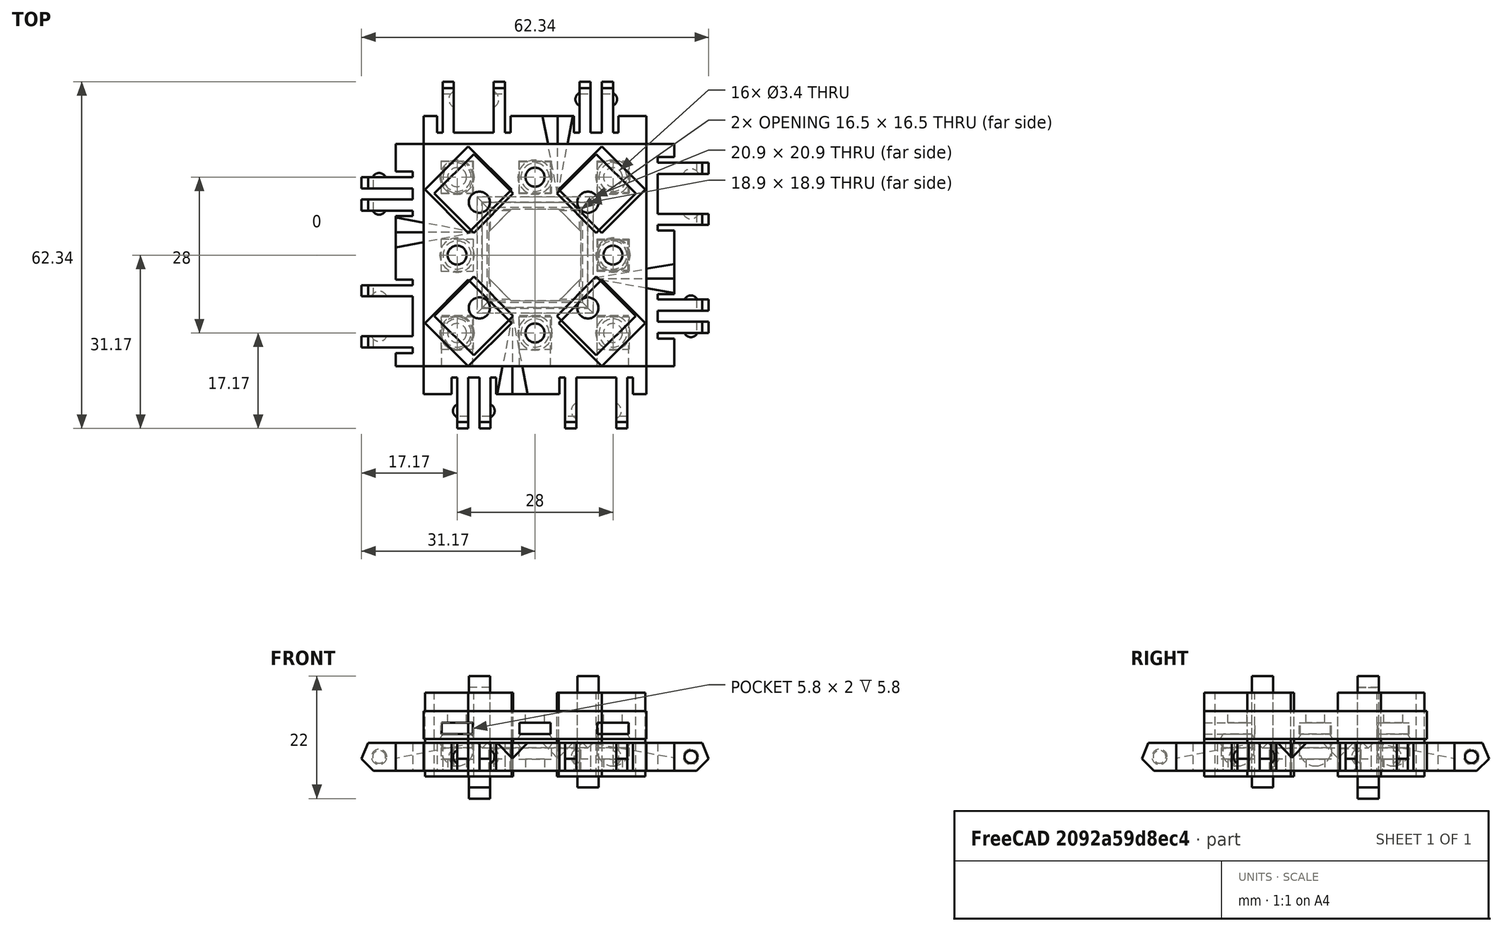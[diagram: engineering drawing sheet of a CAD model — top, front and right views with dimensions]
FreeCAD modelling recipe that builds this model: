
FCSTD DOCUMENT  (FreeCAD 0.17R13522 (Git))
Label: Robot Plates 0.2
License: All rights reserved
LicenseURL: http://en.wikipedia.org/wiki/All_rights_reserved
objects: Part::Box×147, Part::Sphere×51, Part::MultiFuse×48, Part::Cut×47, Part::Cylinder×24, Part::Chamfer×12, Part::Fuse×2, App::DocumentObjectGroup×1
note: 331 computed .brp shape members not serialized (recipe doc carries the construction recipe); baked Part::Feature solids carry a one-line shape summary decoded from their .brp

FEATURE [Part::Box] Box  label="Cube"
  AttacherType = Attacher::AttachEngine3D
  Height = 5
  Length = 40
  Placement = pos=(0,0,-2) rot=(0,0,1;0rad)
  Width = 40
FEATURE [Part::Sphere] Sphere003  label="Mag Hole 3"
  Angle1 = -90
  Angle2 = 90
  Angle3 = 360
  AttacherType = Attacher::AttachEngine3D
  Placement = pos=(6,34,1.7) rot=(0,0,1;0rad)
  Radius = 2.85
FEATURE [Part::Sphere] Sphere005  label="Mag Hole 2"
  Angle1 = -90
  Angle2 = 90
  Angle3 = 360
  AttacherType = Attacher::AttachEngine3D
  Placement = pos=(34,20,1.7) rot=(0,0,1;0rad)
  Radius = 2.85
FEATURE [Part::Sphere] Sphere  label="Mag Hole"
  Angle1 = -90
  Angle2 = 90
  Angle3 = 360
  AttacherType = Attacher::AttachEngine3D
  Placement = pos=(6,6,1.7) rot=(0,0,1;0rad)
  Radius = 2.85
FEATURE [Part::MultiFuse] Fusion004
  Shapes = -> [Sphere,Sphere005,Sphere003]
FEATURE [Part::Cut] Cut003
  Base = -> Box
  Tool = -> Fusion004
FEATURE [Part::Box] Box001  label="Cube001"
  AttacherType = Attacher::AttachEngine3D
  Height = 7
  Length = 5
  Width = 40
FEATURE [Part::Box] Box002  label="Cube002"
  AttacherType = Attacher::AttachEngine3D
  Height = 7
  Length = 10
  Placement = pos=(-10,6,0) rot=(0,0,1;0rad)
  Width = 2
FEATURE [Part::Box] Box003  label="Cube003"
  AttacherType = Attacher::AttachEngine3D
  Height = 7
  Length = 10
  Placement = pos=(-10,10,0) rot=(0,0,1;0rad)
  Width = 2
FEATURE [Part::Box] Box004  label="Cube004"
  AttacherType = Attacher::AttachEngine3D
  Height = 7
  Length = 10
  Placement = pos=(-10,25.4,0) rot=(0,0,1;0rad)
  Width = 2
FEATURE [Part::Box] Box005  label="Cube005"
  AttacherType = Attacher::AttachEngine3D
  Height = 7
  Length = 10
  Placement = pos=(-10,34.6,0) rot=(0,0,1;0rad)
  Width = 2
FEATURE [Part::Sphere] Sphere008
  Angle1 = -90
  Angle2 = 90
  Angle3 = 360
  AttacherType = Attacher::AttachEngine3D
  Placement = pos=(-3,6.5,2.5) rot=(0,0,1;0rad)
  Radius = 1.25
FEATURE [Part::Box] Box006  label="Cube006"
  AttacherType = Attacher::AttachEngine3D
  Height = 10
  Length = 13
  Placement = pos=(-10.19,0,-1.19) rot=(0,-1,0;0.785398rad)
  Width = 40
FEATURE [Part::Sphere] Sphere009
  Angle1 = -90
  Angle2 = 90
  Angle3 = 360
  AttacherType = Attacher::AttachEngine3D
  Placement = pos=(-3,11.5,2.5) rot=(0,0,1;0rad)
  Radius = 1.25
FEATURE [Part::Sphere] Sphere010
  Angle1 = -90
  Angle2 = 90
  Angle3 = 360
  AttacherType = Attacher::AttachEngine3D
  Placement = pos=(-3,28,2.5) rot=(0,0,1;0rad)
  Radius = 1.5
FEATURE [Part::Sphere] Sphere011
  Angle1 = -90
  Angle2 = 90
  Angle3 = 360
  AttacherType = Attacher::AttachEngine3D
  Placement = pos=(-3,34,2.5) rot=(0,0,1;0rad)
  Radius = 1.5
FEATURE [Part::MultiFuse] Fusion
  Shapes = -> [Box001,Box002,Box003,Box004,Box005]
FEATURE [Part::Cut] Cut
  Base = -> Fusion
  Tool = -> Box006
FEATURE [Part::MultiFuse] Fusion001
  Shapes = -> [Sphere008,Sphere009,Cut]
FEATURE [Part::MultiFuse] Fusion002
  Shapes = -> [Sphere011,Sphere010]
FEATURE [Part::Cut] Cut001
  Base = -> Fusion001
  Tool = -> Fusion002
FEATURE [Part::Chamfer] Chamfer001
  Base = -> Cut001
  Edges = 4 edges r=4: [Edge31,Edge37,Edge43,Edge46]
FEATURE [Part::Box] Box007  label="Cube007"
  AttacherType = Attacher::AttachEngine3D
  Height = 7
  Length = 4
  Placement = pos=(-1,5,0) rot=(0,0,1;0rad)
  Width = 1
FEATURE [Part::Box] Box008  label="Cube008"
  AttacherType = Attacher::AttachEngine3D
  Height = 7
  Length = 4
  Placement = pos=(-1,8,0) rot=(0,0,1;0rad)
  Width = 2
FEATURE [Part::Box] Box009  label="Cube009"
  AttacherType = Attacher::AttachEngine3D
  Height = 7
  Length = 4
  Placement = pos=(-1,12,0) rot=(0,0,1;0rad)
  Width = 1
FEATURE [Part::Box] Box010  label="Cube010"
  AttacherType = Attacher::AttachEngine3D
  Height = 7
  Length = 4
  Placement = pos=(-1,24.4,0) rot=(0,0,1;0rad)
  Width = 1
FEATURE [Part::Box] Box011  label="Cube011"
  AttacherType = Attacher::AttachEngine3D
  Height = 7
  Length = 4
  Placement = pos=(-1,36.6,0) rot=(0,0,1;0rad)
  Width = 1
FEATURE [Part::Box] Box012  label="Cube012"
  AttacherType = Attacher::AttachEngine3D
  Height = 7
  Length = 4
  Placement = pos=(-1,27.4,0) rot=(0,0,1;0rad)
  Width = 7.2
FEATURE [Part::MultiFuse] Fusion003
  Shapes = -> [Box012,Box009,Box011,Box008,Box010,Box007]
FEATURE [Part::Cut] Cut002
  Base = -> Chamfer001
  Placement = pos=(-5,40,3) rot=(1,0,0;3.14159rad)
  Tool = -> Fusion003
FEATURE [Part::Box] Box013  label="Cube013"
  AttacherType = Attacher::AttachEngine3D
  Height = 10
  Length = 12
  Placement = pos=(-11,-2,-12) rot=(0,0,1;0rad)
  Width = 44
FEATURE [Part::Cut] Cut004
  Base = -> Cut002
  Tool = -> Box013
FEATURE [Part::Box] Box014  label="Cube014"
  AttacherType = Attacher::AttachEngine3D
  Height = 7
  Length = 10
  Placement = pos=(-10,34.6,0) rot=(0,0,1;0rad)
  Width = 2
FEATURE [Part::Box] Box015  label="Cube015"
  AttacherType = Attacher::AttachEngine3D
  Height = 7
  Length = 5
  Width = 40
FEATURE [Part::Box] Box016  label="Cube016"
  AttacherType = Attacher::AttachEngine3D
  Height = 7
  Length = 10
  Placement = pos=(-10,25.4,0) rot=(0,0,1;0rad)
  Width = 2
FEATURE [Part::Box] Box017  label="Cube017"
  AttacherType = Attacher::AttachEngine3D
  Height = 7
  Length = 10
  Placement = pos=(-10,10,0) rot=(0,0,1;0rad)
  Width = 2
FEATURE [Part::Box] Box018  label="Cube018"
  AttacherType = Attacher::AttachEngine3D
  Height = 7
  Length = 10
  Placement = pos=(-10,6,0) rot=(0,0,1;0rad)
  Width = 2
FEATURE [Part::Sphere] Sphere012
  Angle1 = -90
  Angle2 = 90
  Angle3 = 360
  AttacherType = Attacher::AttachEngine3D
  Placement = pos=(-3,6.5,2.5) rot=(0,0,1;0rad)
  Radius = 1.25
FEATURE [Part::Box] Box019  label="Cube019"
  AttacherType = Attacher::AttachEngine3D
  Height = 10
  Length = 13
  Placement = pos=(-10.19,0,-1.19) rot=(0,-1,0;0.785398rad)
  Width = 40
FEATURE [Part::Sphere] Sphere013
  Angle1 = -90
  Angle2 = 90
  Angle3 = 360
  AttacherType = Attacher::AttachEngine3D
  Placement = pos=(-3,11.5,2.5) rot=(0,0,1;0rad)
  Radius = 1.25
FEATURE [Part::Sphere] Sphere014
  Angle1 = -90
  Angle2 = 90
  Angle3 = 360
  AttacherType = Attacher::AttachEngine3D
  Placement = pos=(-3,28,2.5) rot=(0,0,1;0rad)
  Radius = 1.5
FEATURE [Part::Sphere] Sphere015
  Angle1 = -90
  Angle2 = 90
  Angle3 = 360
  AttacherType = Attacher::AttachEngine3D
  Placement = pos=(-3,34,2.5) rot=(0,0,1;0rad)
  Radius = 1.5
FEATURE [Part::MultiFuse] Fusion005
  Shapes = -> [Box015,Box018,Box017,Box016,Box014]
FEATURE [Part::Cut] Cut005
  Base = -> Fusion005
  Tool = -> Box019
FEATURE [Part::MultiFuse] Fusion006
  Shapes = -> [Sphere012,Sphere013,Cut005]
FEATURE [Part::MultiFuse] Fusion007
  Shapes = -> [Sphere015,Sphere014]
FEATURE [Part::Cut] Cut006
  Base = -> Fusion006
  Tool = -> Fusion007
FEATURE [Part::Chamfer] Chamfer002
  Base = -> Cut006
  Edges = 4 edges r=4: [Edge31,Edge37,Edge43,Edge46]
FEATURE [Part::Box] Box020  label="Cube020"
  AttacherType = Attacher::AttachEngine3D
  Height = 7
  Length = 4
  Placement = pos=(-1,5,0) rot=(0,0,1;0rad)
  Width = 1
FEATURE [Part::Box] Box021  label="Cube021"
  AttacherType = Attacher::AttachEngine3D
  Height = 7
  Length = 4
  Placement = pos=(-1,8,0) rot=(0,0,1;0rad)
  Width = 2
FEATURE [Part::Box] Box022  label="Cube022"
  AttacherType = Attacher::AttachEngine3D
  Height = 7
  Length = 4
  Placement = pos=(-1,12,0) rot=(0,0,1;0rad)
  Width = 1
FEATURE [Part::Box] Box023  label="Cube023"
  AttacherType = Attacher::AttachEngine3D
  Height = 7
  Length = 4
  Placement = pos=(-1,24.4,0) rot=(0,0,1;0rad)
  Width = 1
FEATURE [Part::Box] Box024  label="Cube024"
  AttacherType = Attacher::AttachEngine3D
  Height = 7
  Length = 4
  Placement = pos=(-1,36.6,0) rot=(0,0,1;0rad)
  Width = 1
FEATURE [Part::Box] Box025  label="Cube025"
  AttacherType = Attacher::AttachEngine3D
  Height = 7
  Length = 4
  Placement = pos=(-1,27.4,0) rot=(0,0,1;0rad)
  Width = 7.2
FEATURE [Part::MultiFuse] Fusion008
  Shapes = -> [Box025,Box022,Box024,Box021,Box023,Box020]
FEATURE [Part::Cut] Cut007
  Base = -> Chamfer002
  Placement = pos=(-5,40,3) rot=(1,0,0;3.14159rad)
  Tool = -> Fusion008
FEATURE [Part::Box] Box026  label="Cube026"
  AttacherType = Attacher::AttachEngine3D
  Height = 10
  Length = 12
  Placement = pos=(-11,-2,-12) rot=(0,0,1;0rad)
  Width = 44
FEATURE [Part::Cut] Cut008
  Base = -> Cut007
  Placement = pos=(40,0,0) rot=(0,0,1;1.5708rad)
  Tool = -> Box026
FEATURE [Part::Box] Box027  label="Cube027"
  AttacherType = Attacher::AttachEngine3D
  Height = 7
  Length = 4
  Placement = pos=(-1,12,0) rot=(0,0,1;0rad)
  Width = 1
FEATURE [Part::Box] Box028  label="Cube028"
  AttacherType = Attacher::AttachEngine3D
  Height = 10
  Length = 13
  Placement = pos=(-10.19,0,-1.19) rot=(0,-1,0;0.785398rad)
  Width = 40
FEATURE [Part::Box] Box029  label="Cube029"
  AttacherType = Attacher::AttachEngine3D
  Height = 7
  Length = 4
  Placement = pos=(-1,27.4,0) rot=(0,0,1;0rad)
  Width = 7.2
FEATURE [Part::Box] Box030  label="Cube030"
  AttacherType = Attacher::AttachEngine3D
  Height = 7
  Length = 4
  Placement = pos=(-1,5,0) rot=(0,0,1;0rad)
  Width = 1
FEATURE [Part::Box] Box031  label="Cube031"
  AttacherType = Attacher::AttachEngine3D
  Height = 7
  Length = 10
  Placement = pos=(-10,6,0) rot=(0,0,1;0rad)
  Width = 2
FEATURE [Part::Box] Box032  label="Cube032"
  AttacherType = Attacher::AttachEngine3D
  Height = 10
  Length = 12
  Placement = pos=(-11,-2,-12) rot=(0,0,1;0rad)
  Width = 44
FEATURE [Part::Sphere] Sphere016
  Angle1 = -90
  Angle2 = 90
  Angle3 = 360
  AttacherType = Attacher::AttachEngine3D
  Placement = pos=(-3,6.5,2.5) rot=(0,0,1;0rad)
  Radius = 1.25
FEATURE [Part::Box] Box033  label="Cube033"
  AttacherType = Attacher::AttachEngine3D
  Height = 7
  Length = 10
  Placement = pos=(-10,25.4,0) rot=(0,0,1;0rad)
  Width = 2
FEATURE [Part::Box] Box034  label="Cube034"
  AttacherType = Attacher::AttachEngine3D
  Height = 7
  Length = 10
  Placement = pos=(-10,10,0) rot=(0,0,1;0rad)
  Width = 2
FEATURE [Part::Sphere] Sphere017
  Angle1 = -90
  Angle2 = 90
  Angle3 = 360
  AttacherType = Attacher::AttachEngine3D
  Placement = pos=(-3,28,2.5) rot=(0,0,1;0rad)
  Radius = 1.5
FEATURE [Part::Sphere] Sphere018
  Angle1 = -90
  Angle2 = 90
  Angle3 = 360
  AttacherType = Attacher::AttachEngine3D
  Placement = pos=(-3,11.5,2.5) rot=(0,0,1;0rad)
  Radius = 1.25
FEATURE [Part::Box] Box035  label="Cube035"
  AttacherType = Attacher::AttachEngine3D
  Height = 7
  Length = 4
  Placement = pos=(-1,36.6,0) rot=(0,0,1;0rad)
  Width = 1
FEATURE [Part::Sphere] Sphere019
  Angle1 = -90
  Angle2 = 90
  Angle3 = 360
  AttacherType = Attacher::AttachEngine3D
  Placement = pos=(-3,34,2.5) rot=(0,0,1;0rad)
  Radius = 1.5
FEATURE [Part::MultiFuse] Fusion011
  Shapes = -> [Sphere019,Sphere017]
FEATURE [Part::Box] Box036  label="Cube036"
  AttacherType = Attacher::AttachEngine3D
  Height = 7
  Length = 4
  Placement = pos=(-1,8,0) rot=(0,0,1;0rad)
  Width = 2
FEATURE [Part::Box] Box037  label="Cube037"
  AttacherType = Attacher::AttachEngine3D
  Height = 7
  Length = 10
  Placement = pos=(-10,34.6,0) rot=(0,0,1;0rad)
  Width = 2
FEATURE [Part::Box] Box038  label="Cube038"
  AttacherType = Attacher::AttachEngine3D
  Height = 7
  Length = 4
  Placement = pos=(-1,24.4,0) rot=(0,0,1;0rad)
  Width = 1
FEATURE [Part::MultiFuse] Fusion009
  Shapes = -> [Box029,Box027,Box035,Box036,Box038,Box030]
FEATURE [Part::Box] Box039  label="Cube039"
  AttacherType = Attacher::AttachEngine3D
  Height = 7
  Length = 5
  Width = 40
FEATURE [Part::MultiFuse] Fusion012
  Shapes = -> [Box039,Box031,Box034,Box033,Box037]
FEATURE [Part::Cut] Cut011
  Base = -> Fusion012
  Tool = -> Box028
FEATURE [Part::MultiFuse] Fusion010
  Shapes = -> [Sphere016,Sphere018,Cut011]
FEATURE [Part::Cut] Cut012
  Base = -> Fusion010
  Tool = -> Fusion011
FEATURE [Part::Chamfer] Chamfer003
  Base = -> Cut012
  Edges = 4 edges r=4: [Edge31,Edge37,Edge43,Edge46]
FEATURE [Part::Cut] Cut010
  Base = -> Chamfer003
  Placement = pos=(-5,40,3) rot=(1,0,0;3.14159rad)
  Tool = -> Fusion009
FEATURE [Part::Cut] Cut009
  Base = -> Cut010
  Placement = pos=(40,40,0) rot=(0,0,1;3.14159rad)
  Tool = -> Box032
FEATURE [Part::Sphere] Sphere020
  Angle1 = -90
  Angle2 = 90
  Angle3 = 360
  AttacherType = Attacher::AttachEngine3D
  Placement = pos=(-3,11.5,2.5) rot=(0,0,1;0rad)
  Radius = 1.25
FEATURE [Part::Box] Box040  label="Cube040"
  AttacherType = Attacher::AttachEngine3D
  Height = 7
  Length = 10
  Placement = pos=(-10,6,0) rot=(0,0,1;0rad)
  Width = 2
FEATURE [Part::Box] Box041  label="Cube041"
  AttacherType = Attacher::AttachEngine3D
  Height = 7
  Length = 4
  Placement = pos=(-1,8,0) rot=(0,0,1;0rad)
  Width = 2
FEATURE [Part::Box] Box042  label="Cube042"
  AttacherType = Attacher::AttachEngine3D
  Height = 7
  Length = 10
  Placement = pos=(-10,10,0) rot=(0,0,1;0rad)
  Width = 2
FEATURE [Part::Box] Box043  label="Cube043"
  AttacherType = Attacher::AttachEngine3D
  Height = 10
  Length = 12
  Placement = pos=(-11,-2,-12) rot=(0,0,1;0rad)
  Width = 44
FEATURE [Part::Box] Box044  label="Cube044"
  AttacherType = Attacher::AttachEngine3D
  Height = 7
  Length = 4
  Placement = pos=(-1,5,0) rot=(0,0,1;0rad)
  Width = 1
FEATURE [Part::Sphere] Sphere021
  Angle1 = -90
  Angle2 = 90
  Angle3 = 360
  AttacherType = Attacher::AttachEngine3D
  Placement = pos=(-3,28,2.5) rot=(0,0,1;0rad)
  Radius = 1.5
FEATURE [Part::Sphere] Sphere022
  Angle1 = -90
  Angle2 = 90
  Angle3 = 360
  AttacherType = Attacher::AttachEngine3D
  Placement = pos=(-3,6.5,2.5) rot=(0,0,1;0rad)
  Radius = 1.25
FEATURE [Part::Sphere] Sphere023
  Angle1 = -90
  Angle2 = 90
  Angle3 = 360
  AttacherType = Attacher::AttachEngine3D
  Placement = pos=(-3,34,2.5) rot=(0,0,1;0rad)
  Radius = 1.5
FEATURE [Part::Box] Box045  label="Cube045"
  AttacherType = Attacher::AttachEngine3D
  Height = 7
  Length = 4
  Placement = pos=(-1,12,0) rot=(0,0,1;0rad)
  Width = 1
FEATURE [Part::Box] Box046  label="Cube046"
  AttacherType = Attacher::AttachEngine3D
  Height = 7
  Length = 5
  Width = 40
FEATURE [Part::Box] Box047  label="Cube047"
  AttacherType = Attacher::AttachEngine3D
  Height = 7
  Length = 4
  Placement = pos=(-1,36.6,0) rot=(0,0,1;0rad)
  Width = 1
FEATURE [Part::Box] Box048  label="Cube048"
  AttacherType = Attacher::AttachEngine3D
  Height = 7
  Length = 4
  Placement = pos=(-1,24.4,0) rot=(0,0,1;0rad)
  Width = 1
FEATURE [Part::Box] Box049  label="Cube049"
  AttacherType = Attacher::AttachEngine3D
  Height = 7
  Length = 10
  Placement = pos=(-10,25.4,0) rot=(0,0,1;0rad)
  Width = 2
FEATURE [Part::Box] Box050  label="Cube050"
  AttacherType = Attacher::AttachEngine3D
  Height = 10
  Length = 13
  Placement = pos=(-10.19,0,-1.19) rot=(0,-1,0;0.785398rad)
  Width = 40
FEATURE [Part::Box] Box051  label="Cube051"
  AttacherType = Attacher::AttachEngine3D
  Height = 7
  Length = 10
  Placement = pos=(-10,34.6,0) rot=(0,0,1;0rad)
  Width = 2
FEATURE [Part::MultiFuse] Fusion015
  Shapes = -> [Box046,Box040,Box042,Box049,Box051]
FEATURE [Part::Cut] Cut013
  Base = -> Fusion015
  Tool = -> Box050
FEATURE [Part::MultiFuse] Fusion013
  Shapes = -> [Sphere022,Sphere020,Cut013]
FEATURE [Part::MultiFuse] Fusion016
  Shapes = -> [Sphere023,Sphere021]
FEATURE [Part::Cut] Cut014
  Base = -> Fusion013
  Tool = -> Fusion016
FEATURE [Part::Chamfer] Chamfer004
  Base = -> Cut014
  Edges = 4 edges r=4: [Edge31,Edge37,Edge43,Edge46]
FEATURE [Part::Box] Box052  label="Cube052"
  AttacherType = Attacher::AttachEngine3D
  Height = 7
  Length = 4
  Placement = pos=(-1,27.4,0) rot=(0,0,1;0rad)
  Width = 7.2
FEATURE [Part::MultiFuse] Fusion014
  Shapes = -> [Box052,Box045,Box047,Box041,Box048,Box044]
FEATURE [Part::Cut] Cut016
  Base = -> Chamfer004
  Placement = pos=(-5,40,3) rot=(1,0,0;3.14159rad)
  Tool = -> Fusion014
FEATURE [Part::Cut] Cut015
  Base = -> Cut016
  Placement = pos=(0,40,0) rot=(0,0,-1;1.5708rad)
  Tool = -> Box043
FEATURE [Part::Box] Box054  label="Cube054"
  AttacherType = Attacher::AttachEngine3D
  Height = 15
  Length = 10
  Placement = pos=(9,2,-3) rot=(0,0,1;0.785398rad)
  Width = 10
FEATURE [Part::Box] Box055  label="Cube055"
  AttacherType = Attacher::AttachEngine3D
  Height = 15
  Length = 10
  Placement = pos=(31,24,-3) rot=(0,0,1;0.785398rad)
  Width = 10
FEATURE [Part::Box] Box056  label="Cube056"
  AttacherType = Attacher::AttachEngine3D
  Height = 15
  Length = 10
  Placement = pos=(31,2,-3) rot=(0,0,1;0.785398rad)
  Width = 10
FEATURE [Part::Box] Box057  label="Cube057"
  AttacherType = Attacher::AttachEngine3D
  Height = 15
  Length = 10
  Placement = pos=(9,24,-3) rot=(0,0,1;0.785398rad)
  Width = 10
FEATURE [Part::MultiFuse] Fusion017
  Shapes = -> [Box054,Box057,Box056,Box055]
FEATURE [Part::Box] Box058  label="Cube058"
  AttacherType = Attacher::AttachEngine3D
  Height = 5
  Length = 40
  Placement = pos=(0,0,3.7) rot=(0,0,1;0rad)
  Width = 40
FEATURE [Part::Box] Box059  label="Square Nut Hole 008"
  AttacherType = Attacher::AttachEngine3D
  Height = 2
  Length = 5.6
  Placement = pos=(17.2,31.2,4.6) rot=(0,0,1;0rad)
  Width = 5.6
FEATURE [Part::Box] Box060  label="Square Nut Hole 009"
  AttacherType = Attacher::AttachEngine3D
  Height = 2
  Length = 5.6
  Placement = pos=(17.2,-0.85,4.6) rot=(0,0,1;0rad)
  Width = 10
FEATURE [Part::Box] Box061  label="Square Nut Hole 010"
  AttacherType = Attacher::AttachEngine3D
  Height = 2
  Length = 5.6
  Placement = pos=(31.2,-0.85,4.6) rot=(0,0,1;0rad)
  Width = 10
FEATURE [Part::Box] Box062  label="Square Nut Hole 011"
  AttacherType = Attacher::AttachEngine3D
  Height = 2
  Length = 5.4
  Placement = pos=(31.3,17.3,4.6) rot=(0,0,1;0rad)
  Width = 5.4
FEATURE [Part::Box] Box063  label="Square Nut Hole 012"
  AttacherType = Attacher::AttachEngine3D
  Height = 2
  Length = 5.7
  Placement = pos=(3.15,31.15,4.6) rot=(0,0,1;0rad)
  Width = 5.7
FEATURE [Part::Box] Box064  label="Square Nut Hole 013"
  AttacherType = Attacher::AttachEngine3D
  Height = 2
  Length = 5.5
  Placement = pos=(31.25,31.25,4.6) rot=(0,0,1;0rad)
  Width = 5.5
FEATURE [Part::Box] Box065  label="Square Nut Hole 014"
  AttacherType = Attacher::AttachEngine3D
  Height = 2
  Length = 5.8
  Placement = pos=(3.1,17.1,4.6) rot=(0,0,1;0rad)
  Width = 5.8
FEATURE [Part::Box] Box066  label="Square Nut Hole 015"
  AttacherType = Attacher::AttachEngine3D
  Height = 2
  Length = 5.6
  Placement = pos=(3.2,-0.85,4.6) rot=(0,0,1;0rad)
  Width = 10
FEATURE [Part::Sphere] Sphere006  label="Nut Clearence1"
  Angle1 = -90
  Angle2 = 90
  Angle3 = 360
  AttacherType = Attacher::AttachEngine3D
  Placement = pos=(6,6,2.4) rot=(0,0,1;0rad)
  Radius = 3.35
FEATURE [Part::Sphere] Sphere024
  Angle1 = -90
  Angle2 = 90
  Angle3 = 360
  AttacherType = Attacher::AttachEngine3D
  Placement = pos=(6,34,2.4) rot=(0,0,1;0rad)
  Radius = 3.35
FEATURE [Part::Sphere] Sphere007
  Angle1 = -90
  Angle2 = 90
  Angle3 = 360
  AttacherType = Attacher::AttachEngine3D
  Placement = pos=(34,20,2.4) rot=(0,0,1;0rad)
  Radius = 3.35
FEATURE [Part::Sphere] Sphere001
  Angle1 = -90
  Angle2 = 90
  Angle3 = 360
  AttacherType = Attacher::AttachEngine3D
  Placement = pos=(34,6,2.4) rot=(0,0,1;0rad)
  Radius = 3.35
FEATURE [Part::Sphere] Sphere025
  Angle1 = -90
  Angle2 = 90
  Angle3 = 360
  AttacherType = Attacher::AttachEngine3D
  Placement = pos=(20,6,2.4) rot=(0,0,1;0rad)
  Radius = 3.35
FEATURE [Part::Sphere] Sphere026
  Angle1 = -90
  Angle2 = 90
  Angle3 = 360
  AttacherType = Attacher::AttachEngine3D
  Placement = pos=(20,34,2.4) rot=(0,0,1;0rad)
  Radius = 3.35
FEATURE [Part::Sphere] Sphere004
  Angle1 = -90
  Angle2 = 90
  Angle3 = 360
  AttacherType = Attacher::AttachEngine3D
  Placement = pos=(6,20,2.4) rot=(0,0,1;0rad)
  Radius = 3.35
FEATURE [Part::Sphere] Sphere002
  Angle1 = -90
  Angle2 = 90
  Angle3 = 360
  AttacherType = Attacher::AttachEngine3D
  Placement = pos=(34,34,2.4) rot=(0,0,1;0rad)
  Radius = 3.35
FEATURE [Part::Cylinder] Cylinder
  Angle = 360
  AttacherType = Attacher::AttachEngine3D
  Height = 10
  Placement = pos=(6,6,0) rot=(0,0,1;0rad)
  Radius = 1.7
FEATURE [Part::Cylinder] Cylinder002
  Angle = 360
  AttacherType = Attacher::AttachEngine3D
  Height = 10
  Placement = pos=(34,6,0) rot=(0,0,1;0rad)
  Radius = 1.7
FEATURE [Part::Cylinder] Cylinder001
  Angle = 360
  AttacherType = Attacher::AttachEngine3D
  Height = 10
  Placement = pos=(20,6,0) rot=(0,0,1;0rad)
  Radius = 1.7
FEATURE [Part::Cylinder] Cylinder003
  Angle = 360
  AttacherType = Attacher::AttachEngine3D
  Height = 10
  Placement = pos=(34,34,0) rot=(0,0,1;0rad)
  Radius = 1.7
FEATURE [Part::Cylinder] Cylinder004
  Angle = 360
  AttacherType = Attacher::AttachEngine3D
  Height = 10
  Placement = pos=(20,34,0) rot=(0,0,1;0rad)
  Radius = 1.7
FEATURE [Part::Cylinder] Cylinder005
  Angle = 360
  AttacherType = Attacher::AttachEngine3D
  Height = 10
  Placement = pos=(6,34,0) rot=(0,0,1;0rad)
  Radius = 1.7
FEATURE [Part::Cylinder] Cylinder006
  Angle = 360
  AttacherType = Attacher::AttachEngine3D
  Height = 10
  Placement = pos=(6,20,0) rot=(0,0,1;0rad)
  Radius = 1.7
FEATURE [Part::Cylinder] Cylinder007
  Angle = 360
  AttacherType = Attacher::AttachEngine3D
  Height = 10
  Placement = pos=(34,20,0) rot=(0,0,1;0rad)
  Radius = 1.7
FEATURE [Part::MultiFuse] Fusion018
  Shapes = -> [Cylinder,Cylinder004,Cylinder007,Cylinder005,Cylinder006,Cylinder001,Cylinder002,Cylinder003]
FEATURE [Part::MultiFuse] Fusion019
  Shapes = -> [Sphere007,Sphere024,Sphere006,Sphere025,Sphere001,Sphere026,Sphere004,Sphere002]
FEATURE [Part::MultiFuse] Fusion020
  Shapes = -> [Box061,Box065,Box062,Box063,Box064,Box066,Box059,Box060]
FEATURE [Part::Cut] Cut017
  Base = -> Box058
  Tool = -> Fusion020
FEATURE [Part::Cut] Cut019
  Base = -> Cut017
  Tool = -> Fusion019
FEATURE [Part::Cut] Cut018
  Base = -> Cut019
  Tool = -> Fusion018
FEATURE [Part::Cylinder] Cylinder008
  Angle = 360
  AttacherType = Attacher::AttachEngine3D
  Height = 20
  Placement = pos=(10,10.5,-5) rot=(0,0,1;0rad)
  Radius = 1.9
FEATURE [Part::Cylinder] Cylinder009
  Angle = 360
  AttacherType = Attacher::AttachEngine3D
  Height = 20
  Placement = pos=(29.5,10.5,-5) rot=(0,0,1;0rad)
  Radius = 1.9
FEATURE [Part::Cylinder] Cylinder010
  Angle = 360
  AttacherType = Attacher::AttachEngine3D
  Height = 20
  Placement = pos=(29.5,29.5,-5) rot=(0,0,1;0rad)
  Radius = 1.9
FEATURE [Part::Cylinder] Cylinder011
  Angle = 360
  AttacherType = Attacher::AttachEngine3D
  Height = 20
  Placement = pos=(10,29.5,-7) rot=(0,0,1;0rad)
  Radius = 1.9
FEATURE [Part::MultiFuse] Fusion021  label="M2 Screw holes"
  Shapes = -> [Cylinder008,Cylinder009,Cylinder011,Cylinder010]
FEATURE [Part::Box] Box067  label="Square Nut Hole 016"
  AttacherType = Attacher::AttachEngine3D
  Height = 2
  Length = 5.8
  Placement = pos=(31.1,17.1,4.6) rot=(0,0,1;0rad)
  Width = 5.8
FEATURE [Part::Box] Box068  label="Square Nut Hole 017"
  AttacherType = Attacher::AttachEngine3D
  Height = 2
  Length = 5.8
  Placement = pos=(17.1,3.1,4.6) rot=(0,0,1;0rad)
  Width = 5.8
FEATURE [Part::Box] Box069  label="Square Nut Hole 018"
  AttacherType = Attacher::AttachEngine3D
  Height = 2
  Length = 5.8
  Placement = pos=(31.1,3.1,4.6) rot=(0,0,1;0rad)
  Width = 5.8
FEATURE [Part::Box] Box070  label="Square Nut Hole 019"
  AttacherType = Attacher::AttachEngine3D
  Height = 2
  Length = 5.8
  Placement = pos=(3.1,3.1,4.6) rot=(0,0,1;0rad)
  Width = 5.8
FEATURE [Part::Box] Box071  label="Square Nut Hole 020"
  AttacherType = Attacher::AttachEngine3D
  Height = 2
  Length = 5.8
  Placement = pos=(3.1,31.1,4.6) rot=(0,0,1;0rad)
  Width = 5.8
FEATURE [Part::Box] Box072  label="Square Nut Hole 021"
  AttacherType = Attacher::AttachEngine3D
  Height = 2
  Length = 5.8
  Placement = pos=(17.1,31.1,4.6) rot=(0,0,1;0rad)
  Width = 5.8
FEATURE [Part::Box] Box073  label="Square Nut Hole 022"
  AttacherType = Attacher::AttachEngine3D
  Height = 2
  Length = 5.8
  Placement = pos=(31.1,31.1,4.6) rot=(0,0,1;0rad)
  Width = 5.8
FEATURE [Part::Box] Box074  label="Square Nut Hole 023"
  AttacherType = Attacher::AttachEngine3D
  Height = 2
  Length = 5.8
  Placement = pos=(3.1,17.1,4.6) rot=(0,0,1;0rad)
  Width = 5.8
FEATURE [Part::Cylinder] Cylinder012
  Angle = 360
  AttacherType = Attacher::AttachEngine3D
  Height = 10
  Placement = pos=(6,6,0) rot=(0,0,1;0rad)
  Radius = 1.7
FEATURE [Part::Cylinder] Cylinder013
  Angle = 360
  AttacherType = Attacher::AttachEngine3D
  Height = 10
  Placement = pos=(34,34,0) rot=(0,0,1;0rad)
  Radius = 1.7
FEATURE [Part::Cylinder] Cylinder014
  Angle = 360
  AttacherType = Attacher::AttachEngine3D
  Height = 10
  Placement = pos=(20,34,0) rot=(0,0,1;0rad)
  Radius = 1.7
FEATURE [Part::Cylinder] Cylinder015
  Angle = 360
  AttacherType = Attacher::AttachEngine3D
  Height = 10
  Placement = pos=(6,34,0) rot=(0,0,1;0rad)
  Radius = 1.7
FEATURE [Part::Cylinder] Cylinder016
  Angle = 360
  AttacherType = Attacher::AttachEngine3D
  Height = 10
  Placement = pos=(6,20,0) rot=(0,0,1;0rad)
  Radius = 1.7
FEATURE [Part::Cylinder] Cylinder017
  Angle = 360
  AttacherType = Attacher::AttachEngine3D
  Height = 10
  Placement = pos=(34,20,0) rot=(0,0,1;0rad)
  Radius = 1.7
FEATURE [Part::Cylinder] Cylinder018
  Angle = 360
  AttacherType = Attacher::AttachEngine3D
  Height = 10
  Placement = pos=(34,6,0) rot=(0,0,1;0rad)
  Radius = 1.7
FEATURE [Part::Cylinder] Cylinder019
  Angle = 360
  AttacherType = Attacher::AttachEngine3D
  Height = 10
  Placement = pos=(20,6,0) rot=(0,0,1;0rad)
  Radius = 1.7
FEATURE [Part::Box] Box075  label="Cube059"
  AttacherType = Attacher::AttachEngine3D
  Height = 5
  Length = 40
  Placement = pos=(0,0,-2) rot=(0,0,1;0rad)
  Width = 40
FEATURE [Part::Sphere] Sphere027
  Angle1 = -90
  Angle2 = 90
  Angle3 = 360
  AttacherType = Attacher::AttachEngine3D
  Placement = pos=(34,20,2.4) rot=(0,0,1;0rad)
  Radius = 3.35
FEATURE [Part::Sphere] Sphere028  label="Nut Clearence002"
  Angle1 = -90
  Angle2 = 90
  Angle3 = 360
  AttacherType = Attacher::AttachEngine3D
  Placement = pos=(6,6,2.4) rot=(0,0,1;0rad)
  Radius = 3.35
FEATURE [Part::Sphere] Sphere029
  Angle1 = -90
  Angle2 = 90
  Angle3 = 360
  AttacherType = Attacher::AttachEngine3D
  Placement = pos=(34,34,2.4) rot=(0,0,1;0rad)
  Radius = 3.35
FEATURE [Part::Sphere] Sphere030
  Angle1 = -90
  Angle2 = 90
  Angle3 = 360
  AttacherType = Attacher::AttachEngine3D
  Placement = pos=(34,6,2.4) rot=(0,0,1;0rad)
  Radius = 3.35
FEATURE [Part::Sphere] Sphere031
  Angle1 = -90
  Angle2 = 90
  Angle3 = 360
  AttacherType = Attacher::AttachEngine3D
  Placement = pos=(20,6,2.4) rot=(0,0,1;0rad)
  Radius = 3.35
FEATURE [Part::Sphere] Sphere032
  Angle1 = -90
  Angle2 = 90
  Angle3 = 360
  AttacherType = Attacher::AttachEngine3D
  Placement = pos=(6,34,2.4) rot=(0,0,1;0rad)
  Radius = 3.35
FEATURE [Part::Sphere] Sphere033
  Angle1 = -90
  Angle2 = 90
  Angle3 = 360
  AttacherType = Attacher::AttachEngine3D
  Placement = pos=(6,20,2.4) rot=(0,0,1;0rad)
  Radius = 3.35
FEATURE [Part::Sphere] Sphere034
  Angle1 = -90
  Angle2 = 90
  Angle3 = 360
  AttacherType = Attacher::AttachEngine3D
  Placement = pos=(20,34,2.4) rot=(0,0,1;0rad)
  Radius = 3.35
FEATURE [Part::Box] Box076  label="Cube060"
  AttacherType = Attacher::AttachEngine3D
  Height = 15
  Length = 16.5
  Placement = pos=(11.75,11.75,-3) rot=(0,0,1;0rad)
  Width = 16.5
FEATURE [Part::Box] Box077  label="Cube061"
  AttacherType = Attacher::AttachEngine3D
  Height = 15
  Length = 11
  Placement = pos=(8,24,-3) rot=(0,0,1;0.785398rad)
  Width = 11
FEATURE [Part::Box] Box078  label="Cube062"
  AttacherType = Attacher::AttachEngine3D
  Height = 15
  Length = 11
  Placement = pos=(8,0,-3) rot=(0,0,1;0.785398rad)
  Width = 11
FEATURE [Part::Box] Box079  label="Cube063"
  AttacherType = Attacher::AttachEngine3D
  Height = 15
  Length = 11
  Placement = pos=(32,0,-3) rot=(0,0,1;0.785398rad)
  Width = 11
FEATURE [Part::Box] Box080  label="Cube064"
  AttacherType = Attacher::AttachEngine3D
  Height = 15
  Length = 11
  Placement = pos=(32,24,-3) rot=(0,0,1;0.785398rad)
  Width = 11
FEATURE [Part::MultiFuse] Fusion022
  Shapes = -> [Box078,Box077,Box079,Box080]
FEATURE [Part::Cylinder] Cylinder020
  Angle = 360
  AttacherType = Attacher::AttachEngine3D
  Height = 20
  Placement = pos=(29.5,10.5,-5) rot=(0,0,1;0rad)
  Radius = 1.9
FEATURE [Part::Cylinder] Cylinder021
  Angle = 360
  AttacherType = Attacher::AttachEngine3D
  Height = 20
  Placement = pos=(10,29.5,-7) rot=(0,0,1;0rad)
  Radius = 1.9
FEATURE [Part::Cylinder] Cylinder022
  Angle = 360
  AttacherType = Attacher::AttachEngine3D
  Height = 20
  Placement = pos=(10,10.5,-5) rot=(0,0,1;0rad)
  Radius = 1.9
FEATURE [Part::Cylinder] Cylinder023
  Angle = 360
  AttacherType = Attacher::AttachEngine3D
  Height = 20
  Placement = pos=(29.5,29.5,-5) rot=(0,0,1;0rad)
  Radius = 1.9
FEATURE [Part::MultiFuse] Fusion023  label="M2 Screw holes001"
  Shapes = -> [Cylinder022,Cylinder020,Cylinder021,Cylinder023]
FEATURE [Part::MultiFuse] Fusion024  label="Square Nut Hole"
  Shapes = -> [Box067,Box073,Box071,Box069,Box068,Box070,Box072,Box074]
FEATURE [Part::MultiFuse] Fusion025  label="Square Nut Screw Holes"
  Shapes = -> [Cylinder012,Cylinder018,Cylinder016,Cylinder015,Cylinder014,Cylinder013,Cylinder017,Cylinder019]
FEATURE [Part::MultiFuse] Fusion026  label="Nut Chamfers"
  Shapes = -> [Sphere027,Sphere028,Sphere029,Sphere031,Sphere032,Sphere033,Sphere034,Sphere030]
FEATURE [App::DocumentObjectGroup] Group  label="Cubes"
  Group = -> [Fusion017,Fusion022]
FEATURE [Part::Box] Box082  label="Cube066"
  AttacherType = Attacher::AttachEngine3D
  Height = 10
  Length = 15
  Placement = pos=(30.8481,15.8,2.86019) rot=(0.974848,0.205904,-0.085288;0.803573rad)
  Width = 10
FEATURE [Part::Box] Box083  label="Cube067"
  AttacherType = Attacher::AttachEngine3D
  Height = 10
  Length = 21
  Placement = pos=(9.5,9.5,2.1) rot=(0,0,1;0rad)
  Width = 21
FEATURE [Part::Box] Box084  label="Cube068"
  AttacherType = Attacher::AttachEngine3D
  Height = 14
  Length = 17
  Placement = pos=(11.5,11.5,0) rot=(0,0,1;0rad)
  Width = 17
FEATURE [Part::Cut] Cut020
  Base = -> Box083
  Tool = -> Box084
FEATURE [Part::Chamfer] Chamfer007
  Base = -> Cut020
  Edges = 8 edges r=0.95: [Edge4,Edge5,Edge14,Edge16,Edge17,Edge18,Edge19,Edge20]
FEATURE [Part::Chamfer] Chamfer008
  Base = -> Box076
  Edges = 4 edges r=4: [Edge1,Edge3,Edge5,Edge7]
FEATURE [Part::Box] Box085  label="Cube069"
  AttacherType = Attacher::AttachEngine3D
  Height = 15
  Length = 16
  Placement = pos=(12,12,-13) rot=(0,0,1;0rad)
  Width = 16
FEATURE [Part::Box] Box086  label="Cube070"
  AttacherType = Attacher::AttachEngine3D
  Height = 10
  Length = 10
  Placement = pos=(17,32.0919,9.95) rot=(-0.225436,0.969773,-0.093378;0.807337rad)
  Width = 15
FEATURE [Part::Box] Box087  label="Cube071"
  AttacherType = Attacher::AttachEngine3D
  Height = 10
  Length = 10
  Placement = pos=(7.9081,17,9.95) rot=(-0.450607,0.280623,0.847469;1.65638rad)
  Width = 15
FEATURE [Part::Box] Box088  label="Cube072"
  AttacherType = Attacher::AttachEngine3D
  Height = 10
  Length = 10
  Placement = pos=(23,7.9081,9.95) rot=(-0.381178,-0.08861,0.920245;3.06822rad)
  Width = 15
FEATURE [Part::MultiFuse] Fusion027
  Shapes = -> [Box086,Box082,Box087,Box088]
FEATURE [Part::MultiFuse] Fusion028
  Shapes = -> [Cut015,Cut004,Cut008,Cut009]
FEATURE [Part::Box] Box089  label="Cube073"
  AttacherType = Attacher::AttachEngine3D
  Height = 10
  Length = 10
  Placement = pos=(17,32.0919,9.95) rot=(-0.225436,0.969773,-0.093378;0.807337rad)
  Width = 15
FEATURE [Part::Box] Box090  label="Cube074"
  AttacherType = Attacher::AttachEngine3D
  Height = 10
  Length = 15
  Placement = pos=(30.8481,15.8,2.86019) rot=(0.974848,0.205904,-0.085288;0.803573rad)
  Width = 10
FEATURE [Part::Box] Box091  label="Cube075"
  AttacherType = Attacher::AttachEngine3D
  Height = 10
  Length = 10
  Placement = pos=(7.9081,17,9.95) rot=(-0.450607,0.280623,0.847469;1.65638rad)
  Width = 15
FEATURE [Part::Box] Box092  label="Cube076"
  AttacherType = Attacher::AttachEngine3D
  Height = 10
  Length = 10
  Placement = pos=(23,7.9081,9.95) rot=(-0.381178,-0.08861,0.920245;3.06822rad)
  Width = 15
FEATURE [Part::Box] Box093  label="Cube077"
  AttacherType = Attacher::AttachEngine3D
  Height = 7
  Length = 5
  Width = 40
FEATURE [Part::Box] Box094  label="Cube078"
  AttacherType = Attacher::AttachEngine3D
  Height = 7
  Length = 10
  Placement = pos=(-10,6,0) rot=(0,0,1;0rad)
  Width = 2
FEATURE [Part::Box] Box095  label="Cube079"
  AttacherType = Attacher::AttachEngine3D
  Height = 7
  Length = 10
  Placement = pos=(-10,10,0) rot=(0,0,1;0rad)
  Width = 2
FEATURE [Part::Box] Box096  label="Cube080"
  AttacherType = Attacher::AttachEngine3D
  Height = 7
  Length = 10
  Placement = pos=(-10,25.4,0) rot=(0,0,1;0rad)
  Width = 2
FEATURE [Part::Box] Box097  label="Cube081"
  AttacherType = Attacher::AttachEngine3D
  Height = 7
  Length = 10
  Placement = pos=(-10,34.6,0) rot=(0,0,1;0rad)
  Width = 2
FEATURE [Part::Sphere] Sphere035
  Angle1 = -90
  Angle2 = 90
  Angle3 = 360
  AttacherType = Attacher::AttachEngine3D
  Placement = pos=(-3,6.5,2.5) rot=(0,0,1;0rad)
  Radius = 1.25
FEATURE [Part::Box] Box098  label="Cube082"
  AttacherType = Attacher::AttachEngine3D
  Height = 10
  Length = 13
  Placement = pos=(-10.19,0,-1.19) rot=(0,-1,0;0.785398rad)
  Width = 40
FEATURE [Part::Sphere] Sphere036
  Angle1 = -90
  Angle2 = 90
  Angle3 = 360
  AttacherType = Attacher::AttachEngine3D
  Placement = pos=(-3,11.5,2.5) rot=(0,0,1;0rad)
  Radius = 1.25
FEATURE [Part::Sphere] Sphere037
  Angle1 = -90
  Angle2 = 90
  Angle3 = 360
  AttacherType = Attacher::AttachEngine3D
  Placement = pos=(-3,28,2.5) rot=(0,0,1;0rad)
  Radius = 1.5
FEATURE [Part::Sphere] Sphere038
  Angle1 = -90
  Angle2 = 90
  Angle3 = 360
  AttacherType = Attacher::AttachEngine3D
  Placement = pos=(-3,34,2.5) rot=(0,0,1;0rad)
  Radius = 1.5
FEATURE [Part::MultiFuse] Fusion030
  Shapes = -> [Box093,Box094,Box095,Box096,Box097]
FEATURE [Part::Cut] Cut025
  Base = -> Fusion030
  Tool = -> Box098
FEATURE [Part::MultiFuse] Fusion031
  Shapes = -> [Sphere035,Sphere036,Cut025]
FEATURE [Part::MultiFuse] Fusion032
  Shapes = -> [Sphere038,Sphere037]
FEATURE [Part::Cut] Cut026
  Base = -> Fusion031
  Tool = -> Fusion032
FEATURE [Part::Chamfer] Chamfer009
  Base = -> Cut026
  Edges = 4 edges r=4: [Edge31,Edge37,Edge43,Edge46]
FEATURE [Part::Box] Box099  label="Cube083"
  AttacherType = Attacher::AttachEngine3D
  Height = 7
  Length = 4
  Placement = pos=(-1,5,0) rot=(0,0,1;0rad)
  Width = 1
FEATURE [Part::Box] Box100  label="Cube084"
  AttacherType = Attacher::AttachEngine3D
  Height = 7
  Length = 4
  Placement = pos=(-1,8,0) rot=(0,0,1;0rad)
  Width = 2
FEATURE [Part::Box] Box101  label="Cube085"
  AttacherType = Attacher::AttachEngine3D
  Height = 7
  Length = 4
  Placement = pos=(-1,12,0) rot=(0,0,1;0rad)
  Width = 1
FEATURE [Part::Box] Box102  label="Cube086"
  AttacherType = Attacher::AttachEngine3D
  Height = 7
  Length = 4
  Placement = pos=(-1,24.4,0) rot=(0,0,1;0rad)
  Width = 1
FEATURE [Part::Box] Box103  label="Cube087"
  AttacherType = Attacher::AttachEngine3D
  Height = 7
  Length = 4
  Placement = pos=(-1,36.6,0) rot=(0,0,1;0rad)
  Width = 1
FEATURE [Part::Box] Box104  label="Cube088"
  AttacherType = Attacher::AttachEngine3D
  Height = 7
  Length = 4
  Placement = pos=(-1,27.4,0) rot=(0,0,1;0rad)
  Width = 7.2
FEATURE [Part::MultiFuse] Fusion033
  Shapes = -> [Box104,Box101,Box103,Box100,Box102,Box099]
FEATURE [Part::Cut] Cut027
  Base = -> Chamfer009
  Placement = pos=(-5,40,3) rot=(1,0,0;3.14159rad)
  Tool = -> Fusion033
FEATURE [Part::Box] Box105  label="Cube089"
  AttacherType = Attacher::AttachEngine3D
  Height = 10
  Length = 12
  Placement = pos=(-11,-2,-12) rot=(0,0,1;0rad)
  Width = 44
FEATURE [Part::Cut] Cut028
  Base = -> Cut027
  Tool = -> Box105
FEATURE [Part::Box] Box106  label="Cube090"
  AttacherType = Attacher::AttachEngine3D
  Height = 7
  Length = 10
  Placement = pos=(-10,34.6,0) rot=(0,0,1;0rad)
  Width = 2
FEATURE [Part::Box] Box107  label="Cube091"
  AttacherType = Attacher::AttachEngine3D
  Height = 7
  Length = 5
  Width = 40
FEATURE [Part::Box] Box108  label="Cube092"
  AttacherType = Attacher::AttachEngine3D
  Height = 7
  Length = 10
  Placement = pos=(-10,25.4,0) rot=(0,0,1;0rad)
  Width = 2
FEATURE [Part::Box] Box109  label="Cube093"
  AttacherType = Attacher::AttachEngine3D
  Height = 7
  Length = 10
  Placement = pos=(-10,10,0) rot=(0,0,1;0rad)
  Width = 2
FEATURE [Part::Box] Box110  label="Cube094"
  AttacherType = Attacher::AttachEngine3D
  Height = 7
  Length = 10
  Placement = pos=(-10,6,0) rot=(0,0,1;0rad)
  Width = 2
FEATURE [Part::Sphere] Sphere039
  Angle1 = -90
  Angle2 = 90
  Angle3 = 360
  AttacherType = Attacher::AttachEngine3D
  Placement = pos=(-3,6.5,2.5) rot=(0,0,1;0rad)
  Radius = 1.25
FEATURE [Part::Box] Box111  label="Cube095"
  AttacherType = Attacher::AttachEngine3D
  Height = 10
  Length = 13
  Placement = pos=(-10.19,0,-1.19) rot=(0,-1,0;0.785398rad)
  Width = 40
FEATURE [Part::Sphere] Sphere040
  Angle1 = -90
  Angle2 = 90
  Angle3 = 360
  AttacherType = Attacher::AttachEngine3D
  Placement = pos=(-3,11.5,2.5) rot=(0,0,1;0rad)
  Radius = 1.25
FEATURE [Part::Sphere] Sphere041
  Angle1 = -90
  Angle2 = 90
  Angle3 = 360
  AttacherType = Attacher::AttachEngine3D
  Placement = pos=(-3,28,2.5) rot=(0,0,1;0rad)
  Radius = 1.5
FEATURE [Part::Sphere] Sphere042
  Angle1 = -90
  Angle2 = 90
  Angle3 = 360
  AttacherType = Attacher::AttachEngine3D
  Placement = pos=(-3,34,2.5) rot=(0,0,1;0rad)
  Radius = 1.5
FEATURE [Part::MultiFuse] Fusion034
  Shapes = -> [Box107,Box110,Box109,Box108,Box106]
FEATURE [Part::Cut] Cut029
  Base = -> Fusion034
  Tool = -> Box111
FEATURE [Part::MultiFuse] Fusion035
  Shapes = -> [Sphere039,Sphere040,Cut029]
FEATURE [Part::MultiFuse] Fusion036
  Shapes = -> [Sphere042,Sphere041]
FEATURE [Part::Cut] Cut030
  Base = -> Fusion035
  Tool = -> Fusion036
FEATURE [Part::Chamfer] Chamfer010
  Base = -> Cut030
  Edges = 4 edges r=4: [Edge31,Edge37,Edge43,Edge46]
FEATURE [Part::Box] Box112  label="Cube096"
  AttacherType = Attacher::AttachEngine3D
  Height = 7
  Length = 4
  Placement = pos=(-1,5,0) rot=(0,0,1;0rad)
  Width = 1
FEATURE [Part::Box] Box113  label="Cube097"
  AttacherType = Attacher::AttachEngine3D
  Height = 7
  Length = 4
  Placement = pos=(-1,8,0) rot=(0,0,1;0rad)
  Width = 2
FEATURE [Part::Box] Box114  label="Cube098"
  AttacherType = Attacher::AttachEngine3D
  Height = 7
  Length = 4
  Placement = pos=(-1,12,0) rot=(0,0,1;0rad)
  Width = 1
FEATURE [Part::Box] Box115  label="Cube099"
  AttacherType = Attacher::AttachEngine3D
  Height = 7
  Length = 4
  Placement = pos=(-1,24.4,0) rot=(0,0,1;0rad)
  Width = 1
FEATURE [Part::Box] Box116  label="Cube100"
  AttacherType = Attacher::AttachEngine3D
  Height = 7
  Length = 4
  Placement = pos=(-1,36.6,0) rot=(0,0,1;0rad)
  Width = 1
FEATURE [Part::Box] Box117  label="Cube101"
  AttacherType = Attacher::AttachEngine3D
  Height = 7
  Length = 4
  Placement = pos=(-1,27.4,0) rot=(0,0,1;0rad)
  Width = 7.2
FEATURE [Part::MultiFuse] Fusion037
  Shapes = -> [Box117,Box114,Box116,Box113,Box115,Box112]
FEATURE [Part::Cut] Cut031
  Base = -> Chamfer010
  Placement = pos=(-5,40,3) rot=(1,0,0;3.14159rad)
  Tool = -> Fusion037
FEATURE [Part::Box] Box118  label="Cube102"
  AttacherType = Attacher::AttachEngine3D
  Height = 10
  Length = 12
  Placement = pos=(-11,-2,-12) rot=(0,0,1;0rad)
  Width = 44
FEATURE [Part::Cut] Cut032
  Base = -> Cut031
  Placement = pos=(40,0,0) rot=(0,0,1;1.5708rad)
  Tool = -> Box118
FEATURE [Part::Box] Box119  label="Cube103"
  AttacherType = Attacher::AttachEngine3D
  Height = 7
  Length = 4
  Placement = pos=(-1,12,0) rot=(0,0,1;0rad)
  Width = 1
FEATURE [Part::Box] Box120  label="Cube104"
  AttacherType = Attacher::AttachEngine3D
  Height = 10
  Length = 13
  Placement = pos=(-10.19,0,-1.19) rot=(0,-1,0;0.785398rad)
  Width = 40
FEATURE [Part::Box] Box121  label="Cube105"
  AttacherType = Attacher::AttachEngine3D
  Height = 7
  Length = 4
  Placement = pos=(-1,27.4,0) rot=(0,0,1;0rad)
  Width = 7.2
FEATURE [Part::Box] Box122  label="Cube106"
  AttacherType = Attacher::AttachEngine3D
  Height = 7
  Length = 4
  Placement = pos=(-1,5,0) rot=(0,0,1;0rad)
  Width = 1
FEATURE [Part::Box] Box123  label="Cube107"
  AttacherType = Attacher::AttachEngine3D
  Height = 7
  Length = 10
  Placement = pos=(-10,6,0) rot=(0,0,1;0rad)
  Width = 2
FEATURE [Part::Box] Box124  label="Cube108"
  AttacherType = Attacher::AttachEngine3D
  Height = 10
  Length = 12
  Placement = pos=(-11,-2,-12) rot=(0,0,1;0rad)
  Width = 44
FEATURE [Part::Sphere] Sphere043
  Angle1 = -90
  Angle2 = 90
  Angle3 = 360
  AttacherType = Attacher::AttachEngine3D
  Placement = pos=(-3,6.5,2.5) rot=(0,0,1;0rad)
  Radius = 1.25
FEATURE [Part::Box] Box125  label="Cube109"
  AttacherType = Attacher::AttachEngine3D
  Height = 7
  Length = 10
  Placement = pos=(-10,25.4,0) rot=(0,0,1;0rad)
  Width = 2
FEATURE [Part::Box] Box126  label="Cube110"
  AttacherType = Attacher::AttachEngine3D
  Height = 7
  Length = 10
  Placement = pos=(-10,10,0) rot=(0,0,1;0rad)
  Width = 2
FEATURE [Part::Sphere] Sphere044
  Angle1 = -90
  Angle2 = 90
  Angle3 = 360
  AttacherType = Attacher::AttachEngine3D
  Placement = pos=(-3,28,2.5) rot=(0,0,1;0rad)
  Radius = 1.5
FEATURE [Part::Sphere] Sphere045
  Angle1 = -90
  Angle2 = 90
  Angle3 = 360
  AttacherType = Attacher::AttachEngine3D
  Placement = pos=(-3,11.5,2.5) rot=(0,0,1;0rad)
  Radius = 1.25
FEATURE [Part::Box] Box127  label="Cube111"
  AttacherType = Attacher::AttachEngine3D
  Height = 7
  Length = 4
  Placement = pos=(-1,36.6,0) rot=(0,0,1;0rad)
  Width = 1
FEATURE [Part::Sphere] Sphere046
  Angle1 = -90
  Angle2 = 90
  Angle3 = 360
  AttacherType = Attacher::AttachEngine3D
  Placement = pos=(-3,34,2.5) rot=(0,0,1;0rad)
  Radius = 1.5
FEATURE [Part::MultiFuse] Fusion040
  Shapes = -> [Sphere046,Sphere044]
FEATURE [Part::Box] Box128  label="Cube112"
  AttacherType = Attacher::AttachEngine3D
  Height = 7
  Length = 4
  Placement = pos=(-1,8,0) rot=(0,0,1;0rad)
  Width = 2
FEATURE [Part::Box] Box129  label="Cube113"
  AttacherType = Attacher::AttachEngine3D
  Height = 7
  Length = 10
  Placement = pos=(-10,34.6,0) rot=(0,0,1;0rad)
  Width = 2
FEATURE [Part::Box] Box130  label="Cube114"
  AttacherType = Attacher::AttachEngine3D
  Height = 7
  Length = 4
  Placement = pos=(-1,24.4,0) rot=(0,0,1;0rad)
  Width = 1
FEATURE [Part::MultiFuse] Fusion038
  Shapes = -> [Box121,Box119,Box127,Box128,Box130,Box122]
FEATURE [Part::Box] Box131  label="Cube115"
  AttacherType = Attacher::AttachEngine3D
  Height = 7
  Length = 5
  Width = 40
FEATURE [Part::MultiFuse] Fusion041
  Shapes = -> [Box131,Box123,Box126,Box125,Box129]
FEATURE [Part::Cut] Cut035
  Base = -> Fusion041
  Tool = -> Box120
FEATURE [Part::MultiFuse] Fusion039
  Shapes = -> [Sphere043,Sphere045,Cut035]
FEATURE [Part::Cut] Cut036
  Base = -> Fusion039
  Tool = -> Fusion040
FEATURE [Part::Chamfer] Chamfer011
  Base = -> Cut036
  Edges = 4 edges r=4: [Edge31,Edge37,Edge43,Edge46]
FEATURE [Part::Cut] Cut034
  Base = -> Chamfer011
  Placement = pos=(-5,40,3) rot=(1,0,0;3.14159rad)
  Tool = -> Fusion038
FEATURE [Part::Cut] Cut033
  Base = -> Cut034
  Placement = pos=(40,40,0) rot=(0,0,1;3.14159rad)
  Tool = -> Box124
FEATURE [Part::Sphere] Sphere047
  Angle1 = -90
  Angle2 = 90
  Angle3 = 360
  AttacherType = Attacher::AttachEngine3D
  Placement = pos=(-3,11.5,2.5) rot=(0,0,1;0rad)
  Radius = 1.25
FEATURE [Part::Box] Box132  label="Cube116"
  AttacherType = Attacher::AttachEngine3D
  Height = 7
  Length = 10
  Placement = pos=(-10,6,0) rot=(0,0,1;0rad)
  Width = 2
FEATURE [Part::Box] Box133  label="Cube117"
  AttacherType = Attacher::AttachEngine3D
  Height = 7
  Length = 4
  Placement = pos=(-1,8,0) rot=(0,0,1;0rad)
  Width = 2
FEATURE [Part::Box] Box134  label="Cube118"
  AttacherType = Attacher::AttachEngine3D
  Height = 7
  Length = 10
  Placement = pos=(-10,10,0) rot=(0,0,1;0rad)
  Width = 2
FEATURE [Part::Box] Box135  label="Cube119"
  AttacherType = Attacher::AttachEngine3D
  Height = 10
  Length = 12
  Placement = pos=(-11,-2,-12) rot=(0,0,1;0rad)
  Width = 44
FEATURE [Part::Box] Box136  label="Cube120"
  AttacherType = Attacher::AttachEngine3D
  Height = 7
  Length = 4
  Placement = pos=(-1,5,0) rot=(0,0,1;0rad)
  Width = 1
FEATURE [Part::Sphere] Sphere048
  Angle1 = -90
  Angle2 = 90
  Angle3 = 360
  AttacherType = Attacher::AttachEngine3D
  Placement = pos=(-3,28,2.5) rot=(0,0,1;0rad)
  Radius = 1.5
FEATURE [Part::Sphere] Sphere049
  Angle1 = -90
  Angle2 = 90
  Angle3 = 360
  AttacherType = Attacher::AttachEngine3D
  Placement = pos=(-3,6.5,2.5) rot=(0,0,1;0rad)
  Radius = 1.25
FEATURE [Part::Sphere] Sphere050
  Angle1 = -90
  Angle2 = 90
  Angle3 = 360
  AttacherType = Attacher::AttachEngine3D
  Placement = pos=(-3,34,2.5) rot=(0,0,1;0rad)
  Radius = 1.5
FEATURE [Part::Box] Box137  label="Cube121"
  AttacherType = Attacher::AttachEngine3D
  Height = 7
  Length = 4
  Placement = pos=(-1,12,0) rot=(0,0,1;0rad)
  Width = 1
FEATURE [Part::Box] Box138  label="Cube122"
  AttacherType = Attacher::AttachEngine3D
  Height = 7
  Length = 5
  Width = 40
FEATURE [Part::Box] Box139  label="Cube123"
  AttacherType = Attacher::AttachEngine3D
  Height = 7
  Length = 4
  Placement = pos=(-1,36.6,0) rot=(0,0,1;0rad)
  Width = 1
FEATURE [Part::Box] Box140  label="Cube124"
  AttacherType = Attacher::AttachEngine3D
  Height = 7
  Length = 4
  Placement = pos=(-1,24.4,0) rot=(0,0,1;0rad)
  Width = 1
FEATURE [Part::Box] Box141  label="Cube125"
  AttacherType = Attacher::AttachEngine3D
  Height = 7
  Length = 10
  Placement = pos=(-10,25.4,0) rot=(0,0,1;0rad)
  Width = 2
FEATURE [Part::Box] Box142  label="Cube126"
  AttacherType = Attacher::AttachEngine3D
  Height = 10
  Length = 13
  Placement = pos=(-10.19,0,-1.19) rot=(0,-1,0;0.785398rad)
  Width = 40
FEATURE [Part::Box] Box143  label="Cube127"
  AttacherType = Attacher::AttachEngine3D
  Height = 7
  Length = 10
  Placement = pos=(-10,34.6,0) rot=(0,0,1;0rad)
  Width = 2
FEATURE [Part::MultiFuse] Fusion044
  Shapes = -> [Box138,Box132,Box134,Box141,Box143]
FEATURE [Part::Cut] Cut037
  Base = -> Fusion044
  Tool = -> Box142
FEATURE [Part::MultiFuse] Fusion042
  Shapes = -> [Sphere049,Sphere047,Cut037]
FEATURE [Part::MultiFuse] Fusion045
  Shapes = -> [Sphere050,Sphere048]
FEATURE [Part::Cut] Cut038
  Base = -> Fusion042
  Tool = -> Fusion045
FEATURE [Part::Chamfer] Chamfer012
  Base = -> Cut038
  Edges = 4 edges r=4: [Edge31,Edge37,Edge43,Edge46]
FEATURE [Part::Box] Box144  label="Cube128"
  AttacherType = Attacher::AttachEngine3D
  Height = 7
  Length = 4
  Placement = pos=(-1,27.4,0) rot=(0,0,1;0rad)
  Width = 7.2
FEATURE [Part::MultiFuse] Fusion043
  Shapes = -> [Box144,Box137,Box139,Box133,Box140,Box136]
FEATURE [Part::Cut] Cut040
  Base = -> Chamfer012
  Placement = pos=(-5,40,3) rot=(1,0,0;3.14159rad)
  Tool = -> Fusion043
FEATURE [Part::Cut] Cut039
  Base = -> Cut040
  Placement = pos=(0,40,0) rot=(0,0,-1;1.5708rad)
  Tool = -> Box135
FEATURE [Part::MultiFuse] Fusion046
  Shapes = -> [Cut039,Cut028,Cut032,Cut033]
FEATURE [Part::MultiFuse] Fusion047
  Placement = pos=(0,40,6.7) rot=(1,0,0;3.14159rad)
  Shapes = -> [Fusion026,Fusion024,Fusion025]
FEATURE [Part::MultiFuse] Fusion048
  Shapes = -> [Box089,Box091,Box090,Box092]
FEATURE [Part::Fuse] Fusion049
  Base = -> Box075
  Tool = -> Fusion046
FEATURE [Part::Cut] Cut041
  Base = -> Fusion049
  Tool = -> Fusion047
FEATURE [Part::Cut] Cut042
  Base = -> Cut041
  Tool = -> Fusion048
FEATURE [Part::Box] Box145  label="Cube129"
  AttacherType = Attacher::AttachEngine3D
  Height = 15
  Length = 16
  Placement = pos=(12,12,-13) rot=(0,0,1;0rad)
  Width = 16
FEATURE [Part::Box] Box146  label="Cube130"
  AttacherType = Attacher::AttachEngine3D
  Height = 15
  Length = 16.5
  Placement = pos=(11.75,11.75,-3) rot=(0,0,1;0rad)
  Width = 16.5
FEATURE [Part::Chamfer] Chamfer013
  Base = -> Box146
  Edges = 4 edges r=4: [Edge1,Edge3,Edge5,Edge7]
FEATURE [Part::Box] Box147  label="Cube131"
  AttacherType = Attacher::AttachEngine3D
  Height = 10
  Length = 21
  Placement = pos=(9.5,9.5,2.1) rot=(0,0,1;0rad)
  Width = 21
FEATURE [Part::Box] Box148  label="Cube132"
  AttacherType = Attacher::AttachEngine3D
  Height = 14
  Length = 17
  Placement = pos=(11.5,11.5,0) rot=(0,0,1;0rad)
  Width = 17
FEATURE [Part::Cut] Cut043
  Base = -> Box147
  Tool = -> Box148
FEATURE [Part::Chamfer] Chamfer014
  Base = -> Cut043
  Edges = 8 edges r=0.95: [Edge4,Edge5,Edge14,Edge16,Edge17,Edge18,Edge19,Edge20]
FEATURE [Part::Cut] Cut044
  Base = -> Cut042
  Tool = -> Chamfer014
FEATURE [Part::Cut] Cut045
  Base = -> Cut044
  Tool = -> Chamfer013
FEATURE [Part::Cut] Cut046
  Base = -> Cut045
  Tool = -> Box145
FEATURE [Part::Cut] Cut047
  Base = -> Cut003
  Tool = -> Chamfer007
FEATURE [Part::Cut] Cut048
  Base = -> Cut047
  Tool = -> Chamfer008
FEATURE [Part::Cut] Cut049
  Base = -> Cut048
  Tool = -> Box085
FEATURE [Part::Fuse] Fusion050
  Base = -> Fusion028
  Tool = -> Cut049
FEATURE [Part::Cut] Cut050
  Base = -> Fusion050
  Tool = -> Fusion027
